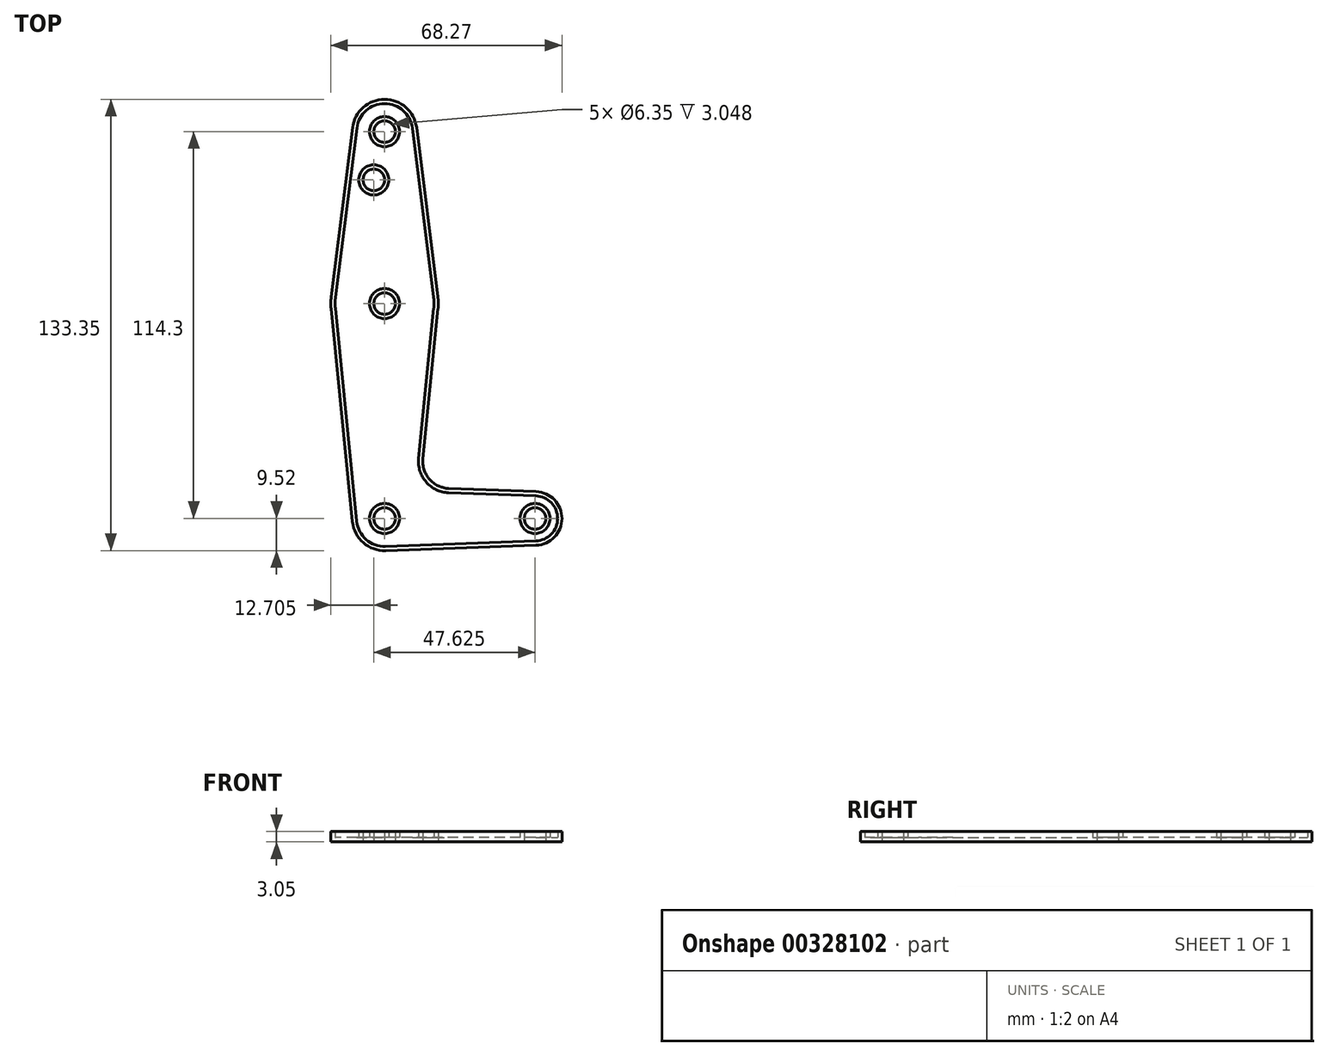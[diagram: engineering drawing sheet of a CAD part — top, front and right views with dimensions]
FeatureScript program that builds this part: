
annotation { "Feature Type Name" : "Feature", "Feature Type Description" : "" }
export const myFeature = defineFeature(function(context is Context, id is Id, definition is map)
    precondition{}
    {
        {
            var Q0;
            Q0=qCreatedBy(makeId("Top.planeOp"),FACE);
            var sketch = newSketch(context, id + "F0", { "sketchPlane" : qUnion([Q0])});
            skLineSegment(sketch, "E0", {"start": v(0, 0) * mm, "end": v(0, 114.3) * mm, "construction": true});
            skLineSegment(sketch, "E1", {"start": v(0, 0) * mm, "end": v(44.45, 0) * mm, "construction": true});
            skCircle(sketch, "E2", {"center": v(0, 114.3) * mm, "radius": 9.53 * mm});
            skCircle(sketch, "E3", {"center": v(44.45, 0) * mm, "radius": 7.94 * mm});
            skCircle(sketch, "E4", {"center": v(0, 63.5) * mm, "radius": 15.88 * mm});
            skCircle(sketch, "E5", {"center": v(0, 0) * mm, "radius": 9.53 * mm});
            skLineSegment(sketch, "E6", {"start": v(9.45, 115.5) * mm, "end": v(15.75, 65.48) * mm});
            skLineSegment(sketch, "E7", {"start": v(-9.45, 115.5) * mm, "end": v(-15.75, 65.48) * mm});
            skCircle(sketch, "E8", {"center": v(0, 114.3) * mm, "radius": 3.18 * mm});
            skCircle(sketch, "E9", {"center": v(0, 63.5) * mm, "radius": 3.18 * mm});
            skCircle(sketch, "E10", {"center": v(0, 0) * mm, "radius": 3.18 * mm});
            skCircle(sketch, "E11", {"center": v(44.45, 0) * mm, "radius": 3.18 * mm});
            skCircle(sketch, "E12", {"center": v(-3.18, 100.03) * mm, "radius": 3.18 * mm});
            skLineSegment(sketch, "E13", {"start": v(-9.48, -0.95) * mm, "end": v(-15.8, 61.91) * mm});
            skLineSegment(sketch, "E14", {"start": v(44.73, -7.93) * mm, "end": v(0.34, -9.52) * mm});
            skLineSegment(sketch, "E15.MirrorCS", {"start": v(11.34, 17.6) * mm, "end": v(15.8, 61.91) * mm});
            skLineSegment(sketch, "E16.MirrorCS", {"start": v(44.73, 7.93) * mm, "end": v(18.97, 8.85) * mm});
            skPoint(sketch, "E17.newPointA", {"position": v(9.48, -0.95) * mm});
            skPoint(sketch, "E17.newPointB", {"position": v(0.34, 9.52) * mm});
            skArc(sketch, "E17.filletArc", {"start": v(11.34, 17.6) * mm, "mid": v(13.26, 11.57) * mm, "end": v(18.97, 8.85) * mm});
            skSolve(sketch);
        }
        {
            var Q0;
            {var subQ0=sQuery(id+"F0.wireOp",EDGE,"E6");Q0=makeQuery(id+"F0.imprint","IMPRINT",FACE,{"disambiguationData":[TD([[makeQuery(id+"F0.imprint","IMPRINT",EDGE,{"derivedFrom":subQ0}),-1.0]])]});}
            var Q1;
            Q1=makeQuery(id+"F0.imprint","IMPRINT",FACE,{"disambiguationData":[TD([[makeQuery(id+"F0.imprint","IMPRINT",EDGE,{"derivedFrom":sQuery(id+"F0.wireOp",EDGE,"E8")}),-1.0]])]});
            var Q2;
            Q2=makeQuery(id+"F0.imprint","IMPRINT",FACE,{"disambiguationData":[TD([[makeQuery(id+"F0.imprint","IMPRINT",EDGE,{"derivedFrom":sQuery(id+"F0.wireOp",EDGE,"E9")}),-1.0]])]});
            var Q3;
            {var subQ0=sQuery(id+"F0.wireOp",EDGE,"E13");Q3=makeQuery(id+"F0.imprint","IMPRINT",FACE,{"disambiguationData":[TD([[makeQuery(id+"F0.imprint","IMPRINT",EDGE,{"derivedFrom":subQ0}),-1.0]])]});}
            var Q4;
            Q4=makeQuery(id+"F0.imprint","IMPRINT",FACE,{"disambiguationData":[TD([[makeQuery(id+"F0.imprint","IMPRINT",EDGE,{"derivedFrom":sQuery(id+"F0.wireOp",EDGE,"E10")}),-1.0]])]});
            var Q5;
            Q5=makeQuery(id+"F0.imprint","IMPRINT",FACE,{"disambiguationData":[TD([[makeQuery(id+"F0.imprint","IMPRINT",EDGE,{"derivedFrom":sQuery(id+"F0.wireOp",EDGE,"E11")}),-1.0]])]});
            extrude(context, id + "F1", {"entities" : qUnion([Q0, Q1, Q2, Q3, Q4, Q5]), "depth" : 3.05 * mm});
        }
        {
            var Q0;
            Q0=makeQuery(id+"F1.opExtrude","CAP_FACE",FACE,{"disambiguationData":[OSD([sQuery(id+"F0.wireOp",EDGE,"E2"),sQuery(id+"F0.wireOp",EDGE,"E3"),sQuery(id+"F0.wireOp",EDGE,"E4"),sQuery(id+"F0.wireOp",EDGE,"E5"),sQuery(id+"F0.wireOp",EDGE,"E6"),sQuery(id+"F0.wireOp",EDGE,"E7"),sQuery(id+"F0.wireOp",EDGE,"E8"),sQuery(id+"F0.wireOp",EDGE,"E9"),sQuery(id+"F0.wireOp",EDGE,"E10"),sQuery(id+"F0.wireOp",EDGE,"E11"),sQuery(id+"F0.wireOp",EDGE,"E12"),sQuery(id+"F0.wireOp",EDGE,"E13"),sQuery(id+"F0.wireOp",EDGE,"E14"),sQuery(id+"F0.wireOp",EDGE,"E15.MirrorCS"),sQuery(id+"F0.wireOp",EDGE,"E16.MirrorCS"),sQuery(id+"F0.wireOp",EDGE,"E17.filletArc")])],"isStart":false});
            shell(context, id + "F2", {"entities" : qUnion([Q0]), "thickness" : 1.27 * mm});
        }
    });
